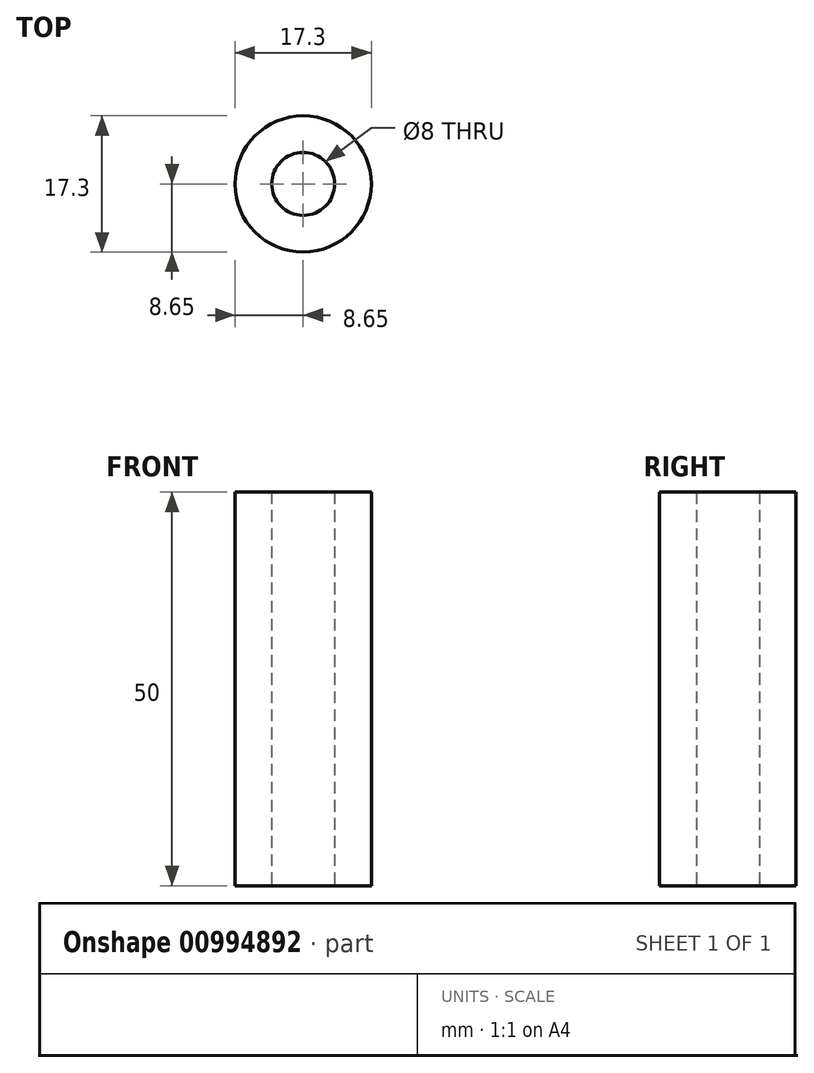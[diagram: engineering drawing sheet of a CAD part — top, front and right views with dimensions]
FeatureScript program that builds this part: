
annotation { "Feature Type Name" : "Feature", "Feature Type Description" : "" }
export const myFeature = defineFeature(function(context is Context, id is Id, definition is map)
    precondition{}
    {
        {
            var Q0;
            Q0=qCreatedBy(makeId("Top.planeOp"), FACE);
            var sketch = newSketch(context, id + "F0", { "sketchPlane" : qUnion([Q0])});
            skCircle(sketch, "E0", {"center": v(0, 0) * mm, "radius": 4 * mm});
            skCircle(sketch, "E1", {"center": v(0, 0) * mm, "radius": 8.65 * mm});
            skSolve(sketch);
        }
        {
            var Q0;
            Q0 = qSketchRegion(id + "F0", true);
            extrude(context, id + "F1", {"entities" : qUnion([Q0]), "depth" : 50 * mm, "offsetDistance" : 25 * mm});
        }
    });
